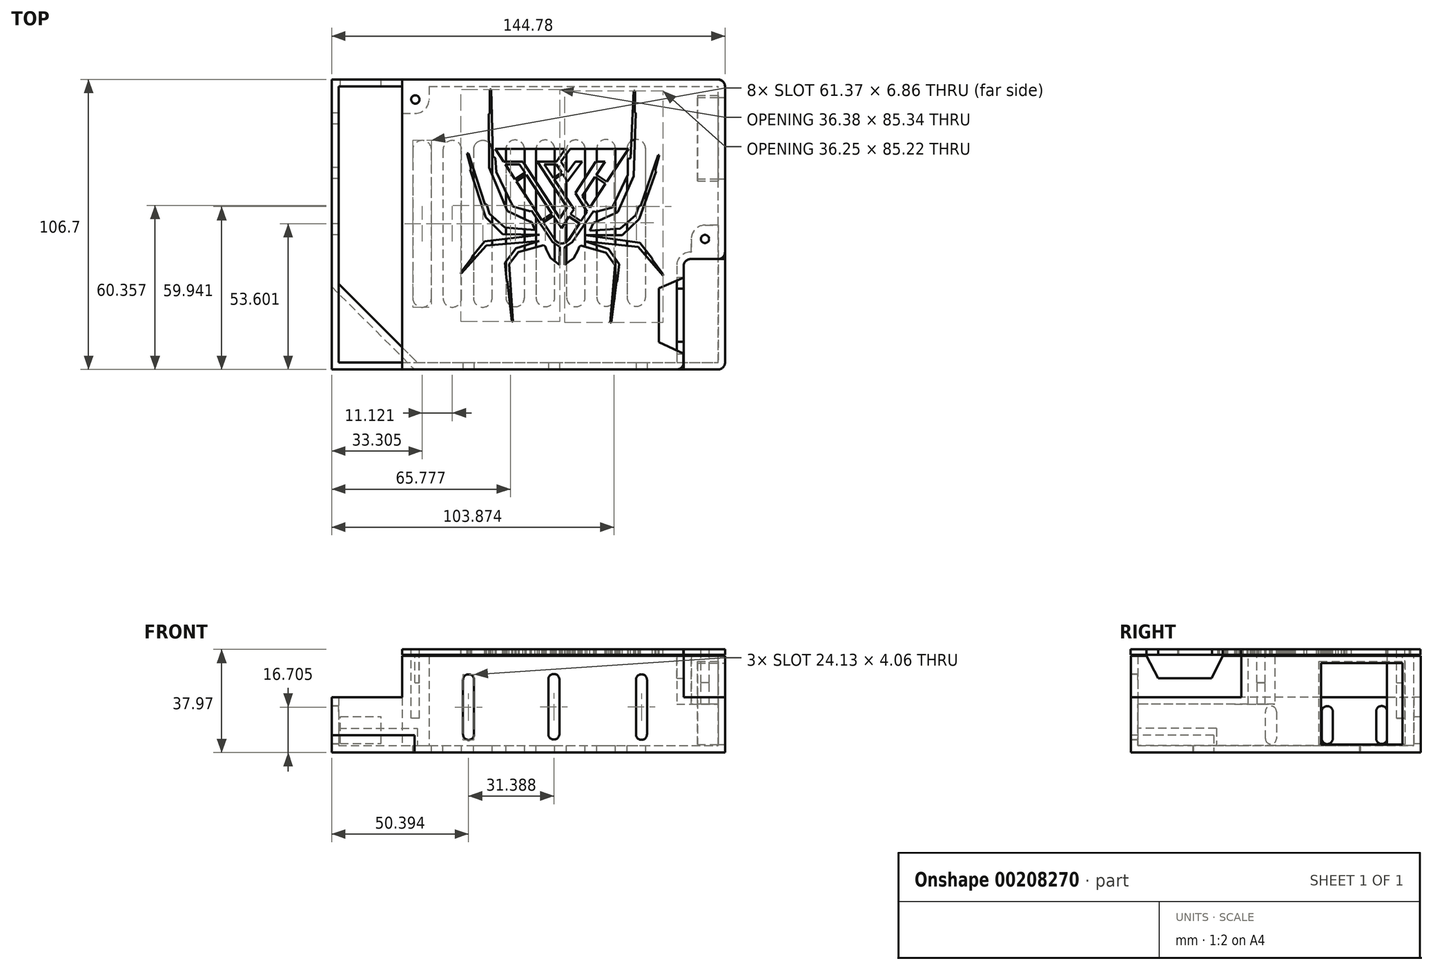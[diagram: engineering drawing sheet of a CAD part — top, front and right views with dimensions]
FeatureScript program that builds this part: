
annotation { "Feature Type Name" : "Feature", "Feature Type Description" : "" }
export const myFeature = defineFeature(function(context is Context, id is Id, definition is map)
    precondition{}
    {
        {
            var Q0;
            Q0=qCreatedBy(makeId("Top.planeOp"),FACE);
            var sketch = newSketch(context, id + "F0", { "sketchPlane" : qUnion([Q0])});
            skLineSegment(sketch, "E0", {"start": v(-77.03, 67.5) * mm, "end": v(67.75, 67.5) * mm});
            skLineSegment(sketch, "E1", {"start": v(67.75, 67.5) * mm, "end": v(67.75, -39.17) * mm});
            skLineSegment(sketch, "E2", {"start": v(-77.03, 67.5) * mm, "end": v(-77.03, -39.17) * mm});
            skLineSegment(sketch, "E3", {"start": v(-77.03, -39.17) * mm, "end": v(67.75, -39.17) * mm});
            skSolve(sketch);
        }
        {
            var Q0;
            Q0 = qSketchRegion(id + "F0", true);
            extrude(context, id + "F1", {"entities" : qUnion([Q0]), "depth" : 35.56 * mm, "offsetDistance" : 25.4 * mm});
        }
        {
            var Q0;
            Q0=makeQuery(id+"F1.opExtrude","CAP_FACE",FACE,{"disambiguationData":[OSD([sQuery(id+"F0.wireOp",EDGE,"E0"),sQuery(id+"F0.wireOp",EDGE,"E1"),sQuery(id+"F0.wireOp",EDGE,"E2"),sQuery(id+"F0.wireOp",EDGE,"E3")])],"isStart":true});
            var sketch = newSketch(context, id + "F2", { "sketchPlane" : qUnion([Q0])});
            skLineSegment(sketch, "E4", {"start": v(-77.03, 39.17) * mm, "end": v(-46.55, 39.17) * mm});
            skLineSegment(sketch, "E5", {"start": v(-77.03, 39.17) * mm, "end": v(-77.03, 8.7) * mm});
            skLineSegment(sketch, "E6", {"start": v(-77.03, 8.7) * mm, "end": v(-46.55, 39.17) * mm});
            skSolve(sketch);
        }
        {
            var Q0;
            Q0 = qSketchRegion(id + "F2", true);
            extrude(context, id + "F3", {"entities" : qUnion([Q0]), "operationType" : NewBodyOperationType.REMOVE, "oppositeDirection" : true, "depth" : 6.35 * mm});
        }
        {
            var Q0;
            Q0=makeQuery(id+"F1.opExtrude","SWEPT_FACE",FACE,{"disambiguationData":[OSD([sQuery(id+"F0.wireOp",EDGE,"E3")])]});
            var sketch = newSketch(context, id + "F4", { "sketchPlane" : qUnion([Q0])});
            skLineSegment(sketch, "E7", {"start": v(67.75, 35.56) * mm, "end": v(52.5, 35.56) * mm});
            skLineSegment(sketch, "E8", {"start": v(52.5, 35.56) * mm, "end": v(52.5, 20.32) * mm});
            skLineSegment(sketch, "E9", {"start": v(52.5, 20.32) * mm, "end": v(67.75, 20.32) * mm});
            skLineSegment(sketch, "E10", {"start": v(67.75, 20.32) * mm, "end": v(67.75, 35.56) * mm});
            skSolve(sketch);
        }
        {
            var Q0;
            Q0 = qSketchRegion(id + "F4", true);
            extrude(context, id + "F5", {"entities" : qUnion([Q0]), "operationType" : NewBodyOperationType.REMOVE, "oppositeDirection" : true, "depth" : 40.64 * mm});
        }
        {
            var Q0;
            Q0=makeQuery(id+"F1.opExtrude","SWEPT_EDGE",EDGE,{"disambiguationData":[OSD([sQuery(id+"F0.wireOp",EDGE,"E1"),sQuery(id+"F0.wireOp",EDGE,"E3")])]});
            var Q1;
            Q1=makeQuery(id+"F5.boolean.opBoolean","COPY",EDGE,{"derivedFrom":makeQuery(id+"F5.opExtrude","CAP_EDGE",EDGE,{"disambiguationData":[OSD([sQuery(id+"F4.wireOp",EDGE,"E8")])],"isStart":true})});
            var Q2;
            Q2=makeQuery(id+"F5.boolean.opBoolean","COPY",EDGE,{"derivedFrom":makeQuery(id+"F5.opExtrude","CAP_EDGE",EDGE,{"disambiguationData":[OSD([sQuery(id+"F4.wireOp",EDGE,"E10")])],"isStart":false})});
            var Q3;
            Q3=makeQuery(id+"F1.opExtrude","SWEPT_EDGE",EDGE,{"disambiguationData":[OSD([sQuery(id+"F0.wireOp",EDGE,"E0"),sQuery(id+"F0.wireOp",EDGE,"E1")])]});
            var Q4;
            Q4=makeQuery(id+"F5.boolean.opBoolean","COPY",EDGE,{"derivedFrom":makeQuery(id+"F5.opExtrude","CAP_EDGE",EDGE,{"disambiguationData":[OSD([sQuery(id+"F4.wireOp",EDGE,"E8")])],"isStart":false})});
            fillet(context, id + "F6", {"entities" : qUnion([Q0, Q1, Q2, Q3, Q4]), "radius" : 2.54 * mm, "tangentPropagation" : true, "allowEdgeOverflow" : false});
        }
        {
            var Q0;
            Q0=makeQuery(id+"F1.opExtrude","CAP_FACE",FACE,{"disambiguationData":[OSD([sQuery(id+"F0.wireOp",EDGE,"E0"),sQuery(id+"F0.wireOp",EDGE,"E1"),sQuery(id+"F0.wireOp",EDGE,"E2"),sQuery(id+"F0.wireOp",EDGE,"E3")])],"isStart":false});
            shell(context, id + "F7", {"entities" : qUnion([Q0]), "thickness" : 2.54 * mm});
        }
        {
            var Q0;
            Q0=makeQuery(id+"F1.opExtrude","SWEPT_FACE",FACE,{"disambiguationData":[OSD([sQuery(id+"F0.wireOp",EDGE,"E3")])]});
            var sketch = newSketch(context, id + "F8", { "sketchPlane" : qUnion([Q0])});
            skLineSegment(sketch, "E11", {"start": v(-77.03, 20.32) * mm, "end": v(-51.05, 20.32) * mm});
            skLineSegment(sketch, "E12", {"start": v(-51.05, 20.32) * mm, "end": v(-51.05, 35.56) * mm});
            skLineSegment(sketch, "E13", {"start": v(-51.05, 35.56) * mm, "end": v(-77.03, 35.56) * mm});
            skLineSegment(sketch, "E14", {"start": v(-77.03, 35.56) * mm, "end": v(-77.03, 20.32) * mm});
            skSolve(sketch);
        }
        {
            var Q0;
            Q0 = qSketchRegion(id + "F8", true);
            extrude(context, id + "F9", {"entities" : qUnion([Q0]), "operationType" : NewBodyOperationType.REMOVE, "oppositeDirection" : true, "depth" : 148.08 * mm});
        }
        {
            var Q0;
            Q0=makeQuery(id+"F5.boolean.opBoolean","COPY",FACE,{"derivedFrom":makeQuery(id+"F5.opExtrude","SWEPT_FACE",FACE,{"disambiguationData":[OSD([sQuery(id+"F4.wireOp",EDGE,"E8")])]})});
            var sketch = newSketch(context, id + "F10", { "sketchPlane" : qUnion([Q0])});
            skLineSegment(sketch, "E15", {"start": v(-33.43, 35.56) * mm, "end": v(-29.05, 27.26) * mm});
            skLineSegment(sketch, "E16", {"start": v(-29.05, 27.26) * mm, "end": v(-9.4, 27.26) * mm});
            skLineSegment(sketch, "E17", {"start": v(-9.4, 27.26) * mm, "end": v(-5.3, 35.56) * mm});
            skLineSegment(sketch, "E18", {"start": v(-5.3, 35.56) * mm, "end": v(-33.43, 35.56) * mm});
            skSolve(sketch);
        }
        {
            var Q0;
            Q0 = qSketchRegion(id + "F10", true);
            extrude(context, id + "F11", {"entities" : qUnion([Q0]), "operationType" : NewBodyOperationType.REMOVE, "oppositeDirection" : true, "depth" : 25.4 * mm});
        }
        {
            var Q0;
            Q0=makeQuery(id+"F1.opExtrude","SWEPT_FACE",FACE,{"disambiguationData":[OSD([sQuery(id+"F0.wireOp",EDGE,"E1")])]});
            var sketch = newSketch(context, id + "F12", { "sketchPlane" : qUnion([Q0])});
            skLineSegment(sketch, "E19.bottom", {"start": v(60.88, 32.96) * mm, "end": v(30.9, 32.96) * mm});
            skLineSegment(sketch, "E19.top", {"start": v(60.88, 2.99) * mm, "end": v(30.9, 2.99) * mm});
            skLineSegment(sketch, "E19.left", {"start": v(60.88, 32.96) * mm, "end": v(60.88, 2.99) * mm});
            skLineSegment(sketch, "E19.right", {"start": v(30.9, 32.96) * mm, "end": v(30.9, 2.99) * mm});
            skSolve(sketch);
        }
        {
            var Q0;
            Q0 = qSketchRegion(id + "F12", true);
            extrude(context, id + "F13", {"entities" : qUnion([Q0]), "operationType" : NewBodyOperationType.REMOVE, "oppositeDirection" : true, "depth" : 25.4 * mm});
        }
        {
            var Q0;
            Q0=makeQuery(id+"F7.opShell","OFFSET_FACE",FACE,{"disambiguationData":[OSD([sQuery(id+"F0.wireOp",EDGE,"E1")])]});
            var sketch = newSketch(context, id + "F14", { "sketchPlane" : qUnion([Q0])});
            skLineSegment(sketch, "E20", {"start": v(-60.88, 32.96) * mm, "end": v(-30.9, 32.96) * mm});
            skLineSegment(sketch, "E21", {"start": v(-30.9, 32.96) * mm, "end": v(-30.9, 2.99) * mm});
            skLineSegment(sketch, "E22", {"start": v(-30.9, 2.99) * mm, "end": v(-30.16, 2.99) * mm});
            skLineSegment(sketch, "E23", {"start": v(-30.16, 2.99) * mm, "end": v(-30.16, 33.5) * mm});
            skLineSegment(sketch, "E24", {"start": v(-30.16, 33.5) * mm, "end": v(-61.7, 33.5) * mm});
            skLineSegment(sketch, "E25", {"start": v(-61.7, 33.5) * mm, "end": v(-61.7, 2.99) * mm});
            skLineSegment(sketch, "E26", {"start": v(-61.7, 2.99) * mm, "end": v(-60.88, 2.99) * mm});
            skLineSegment(sketch, "E27", {"start": v(-60.88, 2.99) * mm, "end": v(-60.88, 32.96) * mm});
            skSolve(sketch);
        }
        {
            var Q0;
            Q0 = qSketchRegion(id + "F14", true);
            extrude(context, id + "F15", {"entities" : qUnion([Q0]), "operationType" : NewBodyOperationType.ADD, "depth" : 7.62 * mm});
        }
        {
            var Q0;
            Q0=makeQuery(id+"F7.opShell","OFFSET_FACE",FACE,{"disambiguationData":[OSD([sQuery(id+"F0.wireOp",EDGE,"E0"),sQuery(id+"F0.wireOp",EDGE,"E1"),sQuery(id+"F0.wireOp",EDGE,"E2"),sQuery(id+"F0.wireOp",EDGE,"E3")])]});
            var sketch = newSketch(context, id + "F16", { "sketchPlane" : qUnion([Q0])});
            skLineSegment(sketch, "E28.bottom", {"start": v(55.31, 13.9) * mm, "end": v(65.22, 13.9) * mm});
            skLineSegment(sketch, "E28.top", {"start": v(55.31, 4) * mm, "end": v(65.22, 4) * mm});
            skLineSegment(sketch, "E28.left", {"start": v(55.31, 13.9) * mm, "end": v(55.31, 4) * mm});
            skLineSegment(sketch, "E28.right", {"start": v(65.22, 13.9) * mm, "end": v(65.22, 4) * mm});
            skLineSegment(sketch, "E29.bottom", {"start": v(-51.05, 64.99) * mm, "end": v(-41.15, 64.99) * mm});
            skLineSegment(sketch, "E29.top", {"start": v(-51.05, 55.08) * mm, "end": v(-41.15, 55.08) * mm});
            skLineSegment(sketch, "E29.left", {"start": v(-51.05, 64.99) * mm, "end": v(-51.05, 55.08) * mm});
            skLineSegment(sketch, "E29.right", {"start": v(-41.15, 64.99) * mm, "end": v(-41.15, 55.08) * mm});
            skSolve(sketch);
        }
        {
            var Q0;
            Q0 = qSketchRegion(id + "F16", true);
            extrude(context, id + "F17", {"entities" : qUnion([Q0]), "operationType" : NewBodyOperationType.ADD, "depth" : 33.02 * mm});
        }
        {
            var Q0;
            Q0=makeQuery(id+"F17.opExtrude","SWEPT_FACE",FACE,{"disambiguationData":[OSD([sQuery(id+"F16.wireOp",EDGE,"E28.left")])]});
            var sketch = newSketch(context, id + "F18", { "sketchPlane" : qUnion([Q0])});
            skLineSegment(sketch, "E30", {"start": v(-4, 2.54) * mm, "end": v(-4, 17.78) * mm});
            skLineSegment(sketch, "E31", {"start": v(-4, 17.78) * mm, "end": v(-13.9, 17.78) * mm});
            skLineSegment(sketch, "E32", {"start": v(-13.9, 17.78) * mm, "end": v(-13.9, 2.54) * mm});
            skLineSegment(sketch, "E33", {"start": v(-13.9, 2.54) * mm, "end": v(-4, 2.54) * mm});
            skSolve(sketch);
        }
        {
            var Q0;
            Q0 = qSketchRegion(id + "F18", true);
            extrude(context, id + "F19", {"entities" : qUnion([Q0]), "operationType" : NewBodyOperationType.REMOVE, "oppositeDirection" : true, "depth" : 9.9 * mm});
        }
        {
            var Q0;
            Q0=makeQuery(id+"F17.opExtrude","SWEPT_EDGE",EDGE,{"disambiguationData":[OSD([sQuery(id+"F16.wireOp",EDGE,"E29.top"),sQuery(id+"F16.wireOp",EDGE,"E29.right")])]});
            var Q1;
            Q1=makeQuery(id+"F17.opExtrude","SWEPT_EDGE",EDGE,{"disambiguationData":[OSD([sQuery(id+"F16.wireOp",EDGE,"E28.bottom"),sQuery(id+"F16.wireOp",EDGE,"E28.left")])]});
            fillet(context, id + "F20", {"entities" : qUnion([Q0, Q1]), "radius" : 5.08 * mm, "tangentPropagation" : true, "allowEdgeOverflow" : false});
        }
        {
            var Q0;
            {var subQ2=sQuery(id+"F0.wireOp",EDGE,"E0");var subQ7=sQuery(id+"F0.wireOp",EDGE,"E1");var subQ8=makeQuery(id+"F1.opExtrude","SWEPT_FACE",FACE,{"disambiguationData":[OSD([subQ2])]});var subQ10=makeQuery(id+"F1.opExtrude","CAP_FACE",FACE,{"disambiguationData":[OSD([subQ2,subQ7,sQuery(id+"F0.wireOp",EDGE,"E2"),sQuery(id+"F0.wireOp",EDGE,"E3")])],"isStart":false});Q0=makeQuery(id+"F17.boolean.opBoolean","MERGE",FACE,{"derivedFrom":[makeQuery(id+"F11.boolean.opBoolean","SPLIT",FACE,{"disambiguationData":[TD([subQ8])],"derivedFrom":subQ10}),makeQuery(id+"F17.opExtrude","CAP_FACE",FACE,{"disambiguationData":[OSD([sQuery(id+"F16.wireOp",EDGE,"E28.bottom"),sQuery(id+"F16.wireOp",EDGE,"E28.top"),sQuery(id+"F16.wireOp",EDGE,"E28.left"),sQuery(id+"F16.wireOp",EDGE,"E28.right")])],"isStart":false}),makeQuery(id+"F17.opExtrude","CAP_FACE",FACE,{"disambiguationData":[OSD([sQuery(id+"F16.wireOp",EDGE,"E29.bottom"),sQuery(id+"F16.wireOp",EDGE,"E29.top"),sQuery(id+"F16.wireOp",EDGE,"E29.left"),sQuery(id+"F16.wireOp",EDGE,"E29.right")])],"isStart":false})]});}
            var sketch = newSketch(context, id + "F21", { "sketchPlane" : qUnion([Q0])});
            skCircle(sketch, "E34", {"center": v(-46.23, 60.16) * mm, "radius": 1.52 * mm});
            skCircle(sketch, "E35", {"center": v(60.4, 8.83) * mm, "radius": 1.52 * mm});
            skSolve(sketch);
        }
        {
            var Q0;
            Q0 = qSketchRegion(id + "F21", true);
            extrude(context, id + "F22", {"entities" : qUnion([Q0]), "operationType" : NewBodyOperationType.REMOVE, "oppositeDirection" : true, "depth" : 9.9 * mm});
        }
        {
            var Q0;
            Q0=makeQuery(id+"F1.opExtrude","SWEPT_FACE",FACE,{"disambiguationData":[OSD([sQuery(id+"F0.wireOp",EDGE,"E0")])]});
            var sketch = newSketch(context, id + "F23", { "sketchPlane" : qUnion([Q0])});
            skLineSegment(sketch, "E36.bottom", {"start": v(73.84, 3.33) * mm, "end": v(58.85, 3.33) * mm});
            skLineSegment(sketch, "E36.top", {"start": v(73.84, 13.24) * mm, "end": v(58.85, 13.24) * mm});
            skLineSegment(sketch, "E36.left", {"start": v(73.84, 3.33) * mm, "end": v(73.84, 13.24) * mm});
            skLineSegment(sketch, "E36.right", {"start": v(58.85, 3.33) * mm, "end": v(58.85, 13.24) * mm});
            skSolve(sketch);
        }
        {
            var Q0;
            Q0 = qSketchRegion(id + "F23", true);
            extrude(context, id + "F24", {"entities" : qUnion([Q0]), "operationType" : NewBodyOperationType.REMOVE, "oppositeDirection" : true, "depth" : 25.4 * mm});
        }
        {
            var Q0;
            Q0=makeQuery(id+"F19.boolean.opBoolean","MERGE",FACE,{"derivedFrom":[makeQuery(id+"F7.opShell","OFFSET_FACE",FACE,{"disambiguationData":[OSD([sQuery(id+"F0.wireOp",EDGE,"E0"),sQuery(id+"F0.wireOp",EDGE,"E1"),sQuery(id+"F0.wireOp",EDGE,"E2"),sQuery(id+"F0.wireOp",EDGE,"E3")])]}),makeQuery(id+"F19.opExtrude","SWEPT_FACE",FACE,{"disambiguationData":[OSD([sQuery(id+"F18.wireOp",EDGE,"E33")])]})]});
            var sketch = newSketch(context, id + "F25", { "sketchPlane" : qUnion([Q0])});
            skLineSegment(sketch, "E37", {"start": v(-47.15, 41.67) * mm, "end": v(-47.15, -12.85) * mm});
            skLineSegment(sketch, "E38", {"start": v(-40.3, -12.85) * mm, "end": v(-40.3, 41.67) * mm});
            skArc(sketch, "E39", {"start": v(-40.3, 41.67) * mm, "mid": v(-43.73, 45.1) * mm, "end": v(-47.15, 41.67) * mm});
            skArc(sketch, "E40", {"start": v(-47.15, -12.85) * mm, "mid": v(-43.73, -16.27) * mm, "end": v(-40.3, -12.85) * mm});
            skLineSegment(sketch, "E41", {"start": v(-36.03, 41.67) * mm, "end": v(-36.03, -12.85) * mm});
            skLineSegment(sketch, "E42", {"start": v(-29.18, -12.85) * mm, "end": v(-29.18, 41.67) * mm});
            skArc(sketch, "E43", {"start": v(-29.18, 41.67) * mm, "mid": v(-32.6, 45.1) * mm, "end": v(-36.03, 41.67) * mm});
            skArc(sketch, "E44", {"start": v(-36.03, -12.85) * mm, "mid": v(-32.6, -16.27) * mm, "end": v(-29.18, -12.85) * mm});
            skLineSegment(sketch, "E45", {"start": v(-24.83, 41.67) * mm, "end": v(-24.83, -12.85) * mm});
            skLineSegment(sketch, "E46", {"start": v(-17.97, -12.85) * mm, "end": v(-17.97, 41.67) * mm});
            skArc(sketch, "E47", {"start": v(-17.97, 41.67) * mm, "mid": v(-21.4, 45.1) * mm, "end": v(-24.83, 41.67) * mm});
            skArc(sketch, "E48", {"start": v(-24.83, -12.85) * mm, "mid": v(-21.4, -16.27) * mm, "end": v(-17.97, -12.85) * mm});
            skLineSegment(sketch, "E49", {"start": v(-12.9, 41.83) * mm, "end": v(-12.9, -12.68) * mm});
            skLineSegment(sketch, "E50", {"start": v(-6.04, -12.68) * mm, "end": v(-6.04, 41.83) * mm});
            skArc(sketch, "E51", {"start": v(-6.04, 41.83) * mm, "mid": v(-9.47, 45.26) * mm, "end": v(-12.9, 41.83) * mm});
            skArc(sketch, "E52", {"start": v(-12.9, -12.68) * mm, "mid": v(-9.47, -16.1) * mm, "end": v(-6.04, -12.68) * mm});
            skLineSegment(sketch, "E53", {"start": v(-1.78, 41.83) * mm, "end": v(-1.78, -12.68) * mm});
            skLineSegment(sketch, "E54", {"start": v(5.08, -12.68) * mm, "end": v(5.08, 41.83) * mm});
            skArc(sketch, "E55", {"start": v(5.08, 41.83) * mm, "mid": v(1.65, 45.26) * mm, "end": v(-1.78, 41.83) * mm});
            skArc(sketch, "E56", {"start": v(-1.78, -12.68) * mm, "mid": v(1.65, -16.1) * mm, "end": v(5.08, -12.68) * mm});
            skLineSegment(sketch, "E57", {"start": v(9.43, 41.83) * mm, "end": v(9.43, -12.68) * mm});
            skLineSegment(sketch, "E58", {"start": v(16.28, -12.68) * mm, "end": v(16.28, 41.83) * mm});
            skArc(sketch, "E59", {"start": v(16.28, 41.83) * mm, "mid": v(12.86, 45.26) * mm, "end": v(9.43, 41.83) * mm});
            skArc(sketch, "E60", {"start": v(9.43, -12.68) * mm, "mid": v(12.86, -16.1) * mm, "end": v(16.28, -12.68) * mm});
            skLineSegment(sketch, "E61", {"start": v(20.55, 42) * mm, "end": v(20.55, -12.51) * mm});
            skLineSegment(sketch, "E62", {"start": v(27.4, -12.51) * mm, "end": v(27.4, 42) * mm});
            skArc(sketch, "E63", {"start": v(27.4, 42) * mm, "mid": v(23.98, 45.43) * mm, "end": v(20.55, 42) * mm});
            skArc(sketch, "E64", {"start": v(20.55, -12.51) * mm, "mid": v(23.98, -15.94) * mm, "end": v(27.4, -12.51) * mm});
            skLineSegment(sketch, "E65", {"start": v(31.67, 42) * mm, "end": v(31.67, -12.51) * mm});
            skLineSegment(sketch, "E66", {"start": v(38.53, -12.51) * mm, "end": v(38.53, 42) * mm});
            skArc(sketch, "E67", {"start": v(38.53, 42) * mm, "mid": v(35.1, 45.43) * mm, "end": v(31.67, 42) * mm});
            skArc(sketch, "E68", {"start": v(31.67, -12.51) * mm, "mid": v(35.1, -15.94) * mm, "end": v(38.53, -12.51) * mm});
            skSolve(sketch);
        }
        {
            var Q0;
            Q0 = qSketchRegion(id + "F25", true);
            extrude(context, id + "F26", {"entities" : qUnion([Q0]), "operationType" : NewBodyOperationType.REMOVE, "oppositeDirection" : true, "depth" : 25.4 * mm});
        }
        {
            var Q0;
            Q0=makeQuery(id+"F1.opExtrude","SWEPT_FACE",FACE,{"disambiguationData":[OSD([sQuery(id+"F0.wireOp",EDGE,"E3")])]});
            var sketch = newSketch(context, id + "F27", { "sketchPlane" : qUnion([Q0])});
            skLineSegment(sketch, "E69", {"start": v(-28.67, 26.74) * mm, "end": v(-28.67, 6.67) * mm});
            skLineSegment(sketch, "E70", {"start": v(-24.6, 6.67) * mm, "end": v(-24.6, 26.74) * mm});
            skArc(sketch, "E71", {"start": v(-24.6, 26.74) * mm, "mid": v(-26.64, 28.77) * mm, "end": v(-28.67, 26.74) * mm});
            skArc(sketch, "E72", {"start": v(-28.67, 6.67) * mm, "mid": v(-26.64, 4.64) * mm, "end": v(-24.6, 6.67) * mm});
            skLineSegment(sketch, "E73", {"start": v(34.98, 26.76) * mm, "end": v(34.98, 6.7) * mm});
            skLineSegment(sketch, "E74", {"start": v(39.04, 6.7) * mm, "end": v(39.04, 26.76) * mm});
            skArc(sketch, "E75", {"start": v(39.04, 26.76) * mm, "mid": v(37, 28.8) * mm, "end": v(34.98, 26.76) * mm});
            skArc(sketch, "E76", {"start": v(34.98, 6.7) * mm, "mid": v(37, 4.66) * mm, "end": v(39.04, 6.7) * mm});
            skLineSegment(sketch, "E77", {"start": v(2.72, 26.87) * mm, "end": v(2.72, 6.8) * mm});
            skLineSegment(sketch, "E78", {"start": v(6.78, 6.8) * mm, "end": v(6.78, 26.87) * mm});
            skArc(sketch, "E79", {"start": v(6.78, 26.87) * mm, "mid": v(4.75, 28.9) * mm, "end": v(2.72, 26.87) * mm});
            skArc(sketch, "E80", {"start": v(2.72, 6.8) * mm, "mid": v(4.75, 4.77) * mm, "end": v(6.78, 6.8) * mm});
            skSolve(sketch);
        }
        {
            var Q0;
            Q0 = qSketchRegion(id + "F27", true);
            extrude(context, id + "F28", {"entities" : qUnion([Q0]), "operationType" : NewBodyOperationType.REMOVE, "oppositeDirection" : true, "depth" : 25.4 * mm});
        }
        {
            var Q0;
            Q0=makeQuery(id+"F1.opExtrude","SWEPT_FACE",FACE,{"disambiguationData":[OSD([sQuery(id+"F0.wireOp",EDGE,"E2")])]});
            var sketch = newSketch(context, id + "F29", { "sketchPlane" : qUnion([Q0])});
            skLineSegment(sketch, "E81", {"start": v(-55.2, 15.1) * mm, "end": v(-55.2, 5.19) * mm});
            skLineSegment(sketch, "E82", {"start": v(-51.13, 5.19) * mm, "end": v(-51.13, 15.1) * mm});
            skArc(sketch, "E83", {"start": v(-51.13, 15.1) * mm, "mid": v(-53.16, 17.13) * mm, "end": v(-55.2, 15.1) * mm});
            skArc(sketch, "E84", {"start": v(-55.2, 5.19) * mm, "mid": v(-53.16, 3.16) * mm, "end": v(-51.13, 5.19) * mm});
            skLineSegment(sketch, "E85", {"start": v(-14.45, 15.05) * mm, "end": v(-14.45, 5.14) * mm});
            skLineSegment(sketch, "E86", {"start": v(-10.38, 5.14) * mm, "end": v(-10.38, 15.05) * mm});
            skArc(sketch, "E87", {"start": v(-10.38, 15.05) * mm, "mid": v(-12.42, 17.08) * mm, "end": v(-14.45, 15.05) * mm});
            skArc(sketch, "E88", {"start": v(-14.45, 5.14) * mm, "mid": v(-12.42, 3.1) * mm, "end": v(-10.38, 5.14) * mm});
            skLineSegment(sketch, "E89", {"start": v(-35.16, 15.05) * mm, "end": v(-35.16, 5.14) * mm});
            skLineSegment(sketch, "E90", {"start": v(-31.1, 5.14) * mm, "end": v(-31.1, 15.05) * mm});
            skArc(sketch, "E91", {"start": v(-31.1, 15.05) * mm, "mid": v(-33.13, 17.08) * mm, "end": v(-35.16, 15.05) * mm});
            skArc(sketch, "E92", {"start": v(-35.16, 5.14) * mm, "mid": v(-33.13, 3.1) * mm, "end": v(-31.1, 5.14) * mm});
            skSolve(sketch);
        }
        {
            var Q0;
            Q0 = qSketchRegion(id + "F29", true);
            extrude(context, id + "F30", {"entities" : qUnion([Q0]), "operationType" : NewBodyOperationType.REMOVE, "oppositeDirection" : true, "depth" : 25.4 * mm});
        }
        {
            var Q0;
            Q0=qCreatedBy(makeId("Top.planeOp"),FACE);
            cPlane(context, id + "F31", {"entities" : qUnion([Q0]), "cplaneType" : CPlaneType.OFFSET, "offset" : 35.94 * mm, "width" : 152.4 * mm, "height" : 152.4 * mm});
        }
        {
            var Q0;
            Q0=qCreatedBy(id+"F31.planeOp",FACE);
            var sketch = newSketch(context, id + "F32", { "sketchPlane" : qUnion([Q0])});
            skLineSegment(sketch, "E93", {"start": v(-51.08, 67.49) * mm, "end": v(67.74, 67.49) * mm});
            skLineSegment(sketch, "E94", {"start": v(67.74, 67.49) * mm, "end": v(67.74, 1.43) * mm});
            skLineSegment(sketch, "E95", {"start": v(67.74, 1.43) * mm, "end": v(52.55, 1.43) * mm});
            skLineSegment(sketch, "E96", {"start": v(52.49, -39.2) * mm, "end": v(-51.08, -39.2) * mm});
            skLineSegment(sketch, "E97", {"start": v(-51.08, -39.2) * mm, "end": v(-51.08, 67.49) * mm});
            skLineSegment(sketch, "E98", {"start": v(52.55, -5.35) * mm, "end": v(43.4, -9.27) * mm});
            skLineSegment(sketch, "E99", {"start": v(52.49, -33.38) * mm, "end": v(43.4, -29.1) * mm});
            skLineSegment(sketch, "E100", {"start": v(43.4, -29.1) * mm, "end": v(43.4, -9.27) * mm});
            skLineSegment(sketch, "E101", {"start": v(52.55, -5.35) * mm, "end": v(52.55, 1.43) * mm});
            skLineSegment(sketch, "E102", {"start": v(52.49, -33.38) * mm, "end": v(52.49, -39.2) * mm});
            skSolve(sketch);
        }
        {
            var Q0;
            Q0 = qSketchRegion(id + "F32", true);
            extrude(context, id + "F33", {"entities" : qUnion([Q0]), "depth" : 2.03 * mm});
        }
        {
            var Q0;
            Q0=makeQuery(id+"F33.opExtrude","SWEPT_EDGE",EDGE,{"disambiguationData":[OSD([sQuery(id+"F32.wireOp",EDGE,"E96"),sQuery(id+"F32.wireOp",EDGE,"E102")])]});
            var Q1;
            Q1=makeQuery(id+"F33.opExtrude","SWEPT_EDGE",EDGE,{"disambiguationData":[OSD([sQuery(id+"F32.wireOp",EDGE,"E94"),sQuery(id+"F32.wireOp",EDGE,"E95")])]});
            var Q2;
            Q2=makeQuery(id+"F33.opExtrude","SWEPT_EDGE",EDGE,{"disambiguationData":[OSD([sQuery(id+"F32.wireOp",EDGE,"E95"),sQuery(id+"F32.wireOp",EDGE,"E101")])]});
            var Q3;
            Q3=makeQuery(id+"F33.opExtrude","SWEPT_EDGE",EDGE,{"disambiguationData":[OSD([sQuery(id+"F32.wireOp",EDGE,"E93"),sQuery(id+"F32.wireOp",EDGE,"E94")])]});
            var Q4;
            Q4=makeQuery(id+"F33.opExtrude","SWEPT_EDGE",EDGE,{"disambiguationData":[OSD([sQuery(id+"F32.wireOp",EDGE,"E94"),sQuery(id+"F32.wireOp",EDGE,"E95")])]});
            fillet(context, id + "F34", {"entities" : qUnion([Q0, Q1, Q2, Q3, Q4]), "radius" : 2.54 * mm, "tangentPropagation" : true, "allowEdgeOverflow" : false});
        }
        {
            var Q0;
            Q0=makeQuery(id+"F33.opExtrude","CAP_FACE",FACE,{"disambiguationData":[OSD([sQuery(id+"F32.wireOp",EDGE,"E93"),sQuery(id+"F32.wireOp",EDGE,"E94"),sQuery(id+"F32.wireOp",EDGE,"E95"),sQuery(id+"F32.wireOp",EDGE,"E96"),sQuery(id+"F32.wireOp",EDGE,"E97"),sQuery(id+"F32.wireOp",EDGE,"E98"),sQuery(id+"F32.wireOp",EDGE,"E99"),sQuery(id+"F32.wireOp",EDGE,"E100"),sQuery(id+"F32.wireOp",EDGE,"E101"),sQuery(id+"F32.wireOp",EDGE,"E102")])],"isStart":false});
            var sketch = newSketch(context, id + "F35", { "sketchPlane" : qUnion([Q0])});
            skCircle(sketch, "E103", {"center": v(-46.24, 60.17) * mm, "radius": 1.53 * mm});
            skCircle(sketch, "E104", {"center": v(60.39, 8.82) * mm, "radius": 1.5 * mm});
            skSolve(sketch);
        }
        {
            var Q0;
            Q0 = qSketchRegion(id + "F35", true);
            extrude(context, id + "F36", {"entities" : qUnion([Q0]), "operationType" : NewBodyOperationType.REMOVE, "oppositeDirection" : true, "depth" : 25.4 * mm});
        }
        {
            var Q0;
            Q0=makeQuery(id+"F33.opExtrude","CAP_FACE",FACE,{"disambiguationData":[OSD([sQuery(id+"F32.wireOp",EDGE,"E93"),sQuery(id+"F32.wireOp",EDGE,"E94"),sQuery(id+"F32.wireOp",EDGE,"E95"),sQuery(id+"F32.wireOp",EDGE,"E96"),sQuery(id+"F32.wireOp",EDGE,"E97"),sQuery(id+"F32.wireOp",EDGE,"E98"),sQuery(id+"F32.wireOp",EDGE,"E99"),sQuery(id+"F32.wireOp",EDGE,"E100"),sQuery(id+"F32.wireOp",EDGE,"E101"),sQuery(id+"F32.wireOp",EDGE,"E102")])],"isStart":false});
            var sketch = newSketch(context, id + "F37", { "sketchPlane" : qUnion([Q0])});
            skPoint(sketch, "E105.endSnap0", {"position": v(7.67, 42.02) * mm});
            skLineSegment(sketch, "E106", {"start": v(-16.85, 42.02) * mm, "end": v(9.01, 42.02) * mm});
            skLineSegment(sketch, "E107", {"start": v(9.01, 42.02) * mm, "end": v(5.67, 37.23) * mm});
            skLineSegment(sketch, "E108", {"start": v(-16.85, 42.02) * mm, "end": v(-13.71, 37.23) * mm});
            skLineSegment(sketch, "E109", {"start": v(-13.1, 36.3) * mm, "end": v(-7.84, 36.3) * mm});
            skLineSegment(sketch, "E110", {"start": v(1.29, 36.3) * mm, "end": v(5.67, 36.3) * mm});
            skArc(sketch, "E111", {"start": v(4.91, 8.8) * mm, "mid": v(7.55, 7.2) * mm, "end": v(10.3, 8.62) * mm});
            skLineSegment(sketch, "E112", {"start": v(7.4, 37.23) * mm, "end": v(10.74, 42.02) * mm});
            skLineSegment(sketch, "E113", {"start": v(10.74, 42.02) * mm, "end": v(32.18, 42.02) * mm});
            skLineSegment(sketch, "E114", {"start": v(18, 20.38) * mm, "end": v(15.25, 24.58) * mm});
            skLineSegment(sketch, "E115", {"start": v(7.4, 37.23) * mm, "end": v(9.84, 33.5) * mm});
            skLineSegment(sketch, "E116", {"start": v(9.84, 33.5) * mm, "end": v(12.63, 37.23) * mm});
            skLineSegment(sketch, "E117", {"start": v(9.75, 30.06) * mm, "end": v(15.18, 37.23) * mm});
            skLineSegment(sketch, "E118", {"start": v(15.18, 37.23) * mm, "end": v(12.63, 37.23) * mm});
            skLineSegment(sketch, "E119", {"start": v(12.63, 25.67) * mm, "end": v(20.2, 37.23) * mm});
            skLineSegment(sketch, "E120", {"start": v(20.2, 37.23) * mm, "end": v(23.54, 37.23) * mm});
            skLineSegment(sketch, "E121", {"start": v(17.05, 18.93) * mm, "end": v(12.63, 25.67) * mm});
            skLineSegment(sketch, "E122", {"start": v(-13.71, 37.23) * mm, "end": v(-6.62, 37.23) * mm});
            skLineSegment(sketch, "E123", {"start": v(-6.62, 37.23) * mm, "end": v(7, 16.45) * mm});
            skLineSegment(sketch, "E124", {"start": v(7, 16.45) * mm, "end": v(9.68, 20.55) * mm});
            skLineSegment(sketch, "E125", {"start": v(9.68, 20.55) * mm, "end": v(-1.25, 37.23) * mm});
            skLineSegment(sketch, "E126", {"start": v(-1.25, 37.23) * mm, "end": v(5.67, 37.23) * mm});
            skLineSegment(sketch, "E127", {"start": v(10.9, 17.94) * mm, "end": v(14.75, 15.42) * mm});
            skLineSegment(sketch, "E128", {"start": v(10.3, 17.03) * mm, "end": v(14.15, 14.5) * mm});
            skLineSegment(sketch, "E129", {"start": v(4.55, 17.4) * mm, "end": v(0.87, 14.98) * mm});
            skLineSegment(sketch, "E130", {"start": v(0.36, 15.75) * mm, "end": v(4.04, 18.17) * mm});
            skLineSegment(sketch, "E131", {"start": v(-9.5, 30.79) * mm, "end": v(-5.8, 33.2) * mm});
            skLineSegment(sketch, "E132", {"start": v(-9.03, 30.08) * mm, "end": v(-5.35, 32.5) * mm});
            skLineSegment(sketch, "E133", {"start": v(4.56, 31.3) * mm, "end": v(7.62, 33.31) * mm});
            skLineSegment(sketch, "E134", {"start": v(4.96, 30.69) * mm, "end": v(8.03, 32.7) * mm});
            skLineSegment(sketch, "E135", {"start": v(19.92, 31.7) * mm, "end": v(23.77, 29.18) * mm});
            skLineSegment(sketch, "E136", {"start": v(20.4, 32.44) * mm, "end": v(24.25, 29.91) * mm});
            skLineSegment(sketch, "E137", {"start": v(-13.1, 36.3) * mm, "end": v(-9.5, 30.79) * mm});
            skLineSegment(sketch, "E138", {"start": v(-7.84, 36.3) * mm, "end": v(-5.8, 33.2) * mm});
            skLineSegment(sketch, "E139", {"start": v(-5.35, 32.5) * mm, "end": v(4.04, 18.17) * mm});
            skLineSegment(sketch, "E140", {"start": v(-9.03, 30.08) * mm, "end": v(0.36, 15.75) * mm});
            skLineSegment(sketch, "E141", {"start": v(4.55, 17.4) * mm, "end": v(7.55, 12.82) * mm});
            skLineSegment(sketch, "E142", {"start": v(0.87, 14.98) * mm, "end": v(4.91, 8.8) * mm});
            skLineSegment(sketch, "E143", {"start": v(12.1, 19.79) * mm, "end": v(4.96, 30.69) * mm});
            skLineSegment(sketch, "E144", {"start": v(4.56, 31.3) * mm, "end": v(1.29, 36.3) * mm});
            skLineSegment(sketch, "E145", {"start": v(5.67, 36.3) * mm, "end": v(7.62, 33.31) * mm});
            skLineSegment(sketch, "E146", {"start": v(8.03, 32.7) * mm, "end": v(9.75, 30.06) * mm});
            skLineSegment(sketch, "E147", {"start": v(32.18, 42.02) * mm, "end": v(24.25, 29.91) * mm});
            skLineSegment(sketch, "E148", {"start": v(23.77, 29.18) * mm, "end": v(18, 20.38) * mm});
            skLineSegment(sketch, "E149", {"start": v(20.4, 32.44) * mm, "end": v(23.54, 37.23) * mm});
            skLineSegment(sketch, "E150", {"start": v(19.92, 31.7) * mm, "end": v(15.25, 24.58) * mm});
            skLineSegment(sketch, "E151", {"start": v(12.1, 19.79) * mm, "end": v(10.9, 17.94) * mm});
            skLineSegment(sketch, "E152", {"start": v(10.3, 17.03) * mm, "end": v(7.55, 12.82) * mm});
            skLineSegment(sketch, "E153", {"start": v(14.15, 14.5) * mm, "end": v(10.3, 8.62) * mm});
            skLineSegment(sketch, "E154", {"start": v(17.05, 18.93) * mm, "end": v(14.75, 15.42) * mm});
            skSolve(sketch);
        }
        {
            var Q0;
            Q0 = qSketchRegion(id + "F37", true);
            extrude(context, id + "F38", {"entities" : qUnion([Q0]), "operationType" : NewBodyOperationType.REMOVE, "oppositeDirection" : true, "depth" : 25.4 * mm});
        }
        {
            var Q0;
            Q0=makeQuery(id+"F33.opExtrude","CAP_FACE",FACE,{"disambiguationData":[OSD([sQuery(id+"F32.wireOp",EDGE,"E93"),sQuery(id+"F32.wireOp",EDGE,"E94"),sQuery(id+"F32.wireOp",EDGE,"E95"),sQuery(id+"F32.wireOp",EDGE,"E96"),sQuery(id+"F32.wireOp",EDGE,"E97"),sQuery(id+"F32.wireOp",EDGE,"E98"),sQuery(id+"F32.wireOp",EDGE,"E99"),sQuery(id+"F32.wireOp",EDGE,"E100"),sQuery(id+"F32.wireOp",EDGE,"E101"),sQuery(id+"F32.wireOp",EDGE,"E102")])],"isStart":false});
            var sketch = newSketch(context, id + "F39", { "sketchPlane" : qUnion([Q0])});
            skPoint(sketch, "E155.endSnap0", {"position": v(8.54, 25.24) * mm});
            skLineSegment(sketch, "E156", {"start": v(19.4, 19.08) * mm, "end": v(19.87, 18.77) * mm});
            skLineSegment(sketch, "E157", {"start": v(19.87, 18.77) * mm, "end": v(19.87, 18.7) * mm});
            skLineSegment(sketch, "E158", {"start": v(19.87, 18.7) * mm, "end": v(26.3, 20.38) * mm});
            skLineSegment(sketch, "E159", {"start": v(26.3, 20.38) * mm, "end": v(32.03, 32.47) * mm});
            skLineSegment(sketch, "E160", {"start": v(32.03, 32.47) * mm, "end": v(32.01, 38.3) * mm});
            skLineSegment(sketch, "E161", {"start": v(32.01, 38.3) * mm, "end": v(32.98, 38.53) * mm});
            skLineSegment(sketch, "E162", {"start": v(32.98, 38.53) * mm, "end": v(34.18, 63.36) * mm});
            skLineSegment(sketch, "E163", {"start": v(34.18, 63.36) * mm, "end": v(34.6, 63.34) * mm});
            skLineSegment(sketch, "E164", {"start": v(34.6, 63.34) * mm, "end": v(34.5, 55.45) * mm});
            skLineSegment(sketch, "E165", {"start": v(34.5, 55.45) * mm, "end": v(34.85, 55.14) * mm});
            skLineSegment(sketch, "E166", {"start": v(34.85, 55.14) * mm, "end": v(34.18, 31.9) * mm});
            skLineSegment(sketch, "E167", {"start": v(34.18, 31.9) * mm, "end": v(28.34, 18.7) * mm});
            skLineSegment(sketch, "E168", {"start": v(28.34, 18.7) * mm, "end": v(19.87, 14.92) * mm});
            skLineSegment(sketch, "E169", {"start": v(19.87, 14.92) * mm, "end": v(19.4, 14.93) * mm});
            skLineSegment(sketch, "E170", {"start": v(19.4, 14.93) * mm, "end": v(18, 11.92) * mm});
            skLineSegment(sketch, "E171", {"start": v(18, 11.92) * mm, "end": v(29.13, 12.59) * mm});
            skLineSegment(sketch, "E172", {"start": v(29.13, 12.59) * mm, "end": v(34.85, 17.61) * mm});
            skLineSegment(sketch, "E173", {"start": v(34.85, 17.61) * mm, "end": v(36.04, 20.97) * mm});
            skLineSegment(sketch, "E174", {"start": v(36.04, 20.97) * mm, "end": v(36.67, 20.95) * mm});
            skLineSegment(sketch, "E175", {"start": v(36.67, 20.95) * mm, "end": v(43.11, 39.69) * mm});
            skLineSegment(sketch, "E176", {"start": v(43.11, 39.69) * mm, "end": v(43.59, 39.68) * mm});
            skLineSegment(sketch, "E177", {"start": v(43.59, 39.68) * mm, "end": v(41.97, 33.98) * mm});
            skLineSegment(sketch, "E178", {"start": v(41.97, 33.98) * mm, "end": v(42.36, 33.7) * mm});
            skLineSegment(sketch, "E179", {"start": v(42.36, 33.7) * mm, "end": v(36.21, 16.25) * mm});
            skLineSegment(sketch, "E180", {"start": v(36.21, 16.25) * mm, "end": v(29.96, 10.2) * mm});
            skLineSegment(sketch, "E181", {"start": v(29.96, 10.2) * mm, "end": v(16.4, 10.2) * mm});
            skLineSegment(sketch, "E182", {"start": v(16.4, 10.2) * mm, "end": v(36.47, 7.39) * mm});
            skLineSegment(sketch, "E183", {"start": v(36.47, 7.39) * mm, "end": v(41.05, 1.63) * mm});
            skLineSegment(sketch, "E184", {"start": v(41.05, 1.63) * mm, "end": v(41.05, 1.2) * mm});
            skLineSegment(sketch, "E185", {"start": v(41.05, 1.2) * mm, "end": v(44.97, -4.18) * mm});
            skLineSegment(sketch, "E186", {"start": v(44.97, -4.18) * mm, "end": v(44.93, -4.64) * mm});
            skLineSegment(sketch, "E187", {"start": v(44.93, -4.64) * mm, "end": v(35.81, 5.93) * mm});
            skLineSegment(sketch, "E188", {"start": v(35.81, 5.93) * mm, "end": v(16.4, 7.92) * mm});
            skLineSegment(sketch, "E189", {"start": v(16.4, 7.92) * mm, "end": v(24.85, 5.09) * mm});
            skLineSegment(sketch, "E190", {"start": v(24.85, 5.09) * mm, "end": v(28.83, -0.38) * mm});
            skLineSegment(sketch, "E191", {"start": v(28.83, -0.38) * mm, "end": v(28, -6.9) * mm});
            skLineSegment(sketch, "E192", {"start": v(28, -6.9) * mm, "end": v(27.78, -7.05) * mm});
            skLineSegment(sketch, "E193", {"start": v(27.78, -7.05) * mm, "end": v(25.9, -21.86) * mm});
            skLineSegment(sketch, "E194", {"start": v(25.5, -21.86) * mm, "end": v(27.34, -0.87) * mm});
            skLineSegment(sketch, "E195", {"start": v(25.5, -21.86) * mm, "end": v(25.9, -21.86) * mm});
            skLineSegment(sketch, "E196", {"start": v(27.34, -0.87) * mm, "end": v(23.93, 3.74) * mm});
            skLineSegment(sketch, "E197", {"start": v(23.93, 3.74) * mm, "end": v(14.74, 6.47) * mm});
            skLineSegment(sketch, "E198", {"start": v(14.74, 6.47) * mm, "end": v(14.08, 5.97) * mm});
            skLineSegment(sketch, "E199", {"start": v(14.08, 5.97) * mm, "end": v(13.65, 4.8) * mm});
            skLineSegment(sketch, "E200", {"start": v(13.65, 4.8) * mm, "end": v(12.05, 1.7) * mm});
            skLineSegment(sketch, "E201", {"start": v(12.05, 1.7) * mm, "end": v(10.37, 0.58) * mm});
            skLineSegment(sketch, "E202", {"start": v(10.37, 0.58) * mm, "end": v(8.72, -0.65) * mm});
            skLineSegment(sketch, "E203", {"start": v(11.5, 7.65) * mm, "end": v(19.4, 19.08) * mm});
            skLineSegment(sketch, "E204.MirrorCS", {"start": v(-10.32, -21.5) * mm, "end": v(-10.73, -21.5) * mm});
            skLineSegment(sketch, "E205.MirrorCS", {"start": v(-29.44, -3.45) * mm, "end": v(-29.4, -3.9) * mm});
            skLineSegment(sketch, "E206.MirrorCS", {"start": v(-3.42, 19.3) * mm, "end": v(-3.9, 19) * mm});
            skLineSegment(sketch, "E207.MirrorCS", {"start": v(-3.97, 15.15) * mm, "end": v(-3.5, 15.16) * mm});
            skLineSegment(sketch, "E208.MirrorCS", {"start": v(-25.69, 34.65) * mm, "end": v(-26.09, 34.38) * mm});
            skLineSegment(sketch, "E209.MirrorCS", {"start": v(-3.9, 19) * mm, "end": v(-3.9, 18.94) * mm});
            skLineSegment(sketch, "E210.MirrorCS", {"start": v(-18.35, 63.84) * mm, "end": v(-18.78, 63.83) * mm});
            skLineSegment(sketch, "E211.MirrorCS", {"start": v(1.64, 6.09) * mm, "end": v(2.05, 4.9) * mm});
            skLineSegment(sketch, "E212.MirrorCS", {"start": v(-20.02, 21.52) * mm, "end": v(-20.65, 21.52) * mm});
            skLineSegment(sketch, "E213.MirrorCS", {"start": v(-11.75, -0.49) * mm, "end": v(-8.25, 4.06) * mm});
            skLineSegment(sketch, "E214.MirrorCS", {"start": v(-9.14, 5.42) * mm, "end": v(-13.23, 0.03) * mm});
            skLineSegment(sketch, "E215.MirrorCS", {"start": v(-18.9, 18.14) * mm, "end": v(-20.02, 21.52) * mm});
            skLineSegment(sketch, "E216.MirrorCS", {"start": v(-16.78, 38.54) * mm, "end": v(-17.65, 39.28) * mm});
            skLineSegment(sketch, "E217.MirrorCS", {"start": v(5.25, 0.63) * mm, "end": v(6.87, -0.63) * mm});
            skLineSegment(sketch, "E218.MirrorCS", {"start": v(-16.4, 33.53) * mm, "end": v(-16.78, 38.54) * mm});
            skLineSegment(sketch, "E219.MirrorCS", {"start": v(0.99, 6.61) * mm, "end": v(1.64, 6.09) * mm});
            skLineSegment(sketch, "E220.MirrorCS", {"start": v(-3.5, 15.16) * mm, "end": v(-2.16, 12.12) * mm});
            skLineSegment(sketch, "E221.MirrorCS", {"start": v(-25.41, 2.28) * mm, "end": v(-25.42, 1.86) * mm});
            skLineSegment(sketch, "E222.MirrorCS", {"start": v(2.05, 4.9) * mm, "end": v(3.59, 1.8) * mm});
            skLineSegment(sketch, "E223.MirrorCS", {"start": v(3.59, 1.8) * mm, "end": v(5.25, 0.63) * mm});
            skLineSegment(sketch, "E224.MirrorCS", {"start": v(-26.72, 40.38) * mm, "end": v(-27.2, 40.37) * mm});
            skLineSegment(sketch, "E225.MirrorCS", {"start": v(-12.54, -6.5) * mm, "end": v(-12.3, -6.65) * mm});
            skLineSegment(sketch, "E226.MirrorCS", {"start": v(-25.42, 1.86) * mm, "end": v(-29.44, -3.45) * mm});
            skLineSegment(sketch, "E227.MirrorCS", {"start": v(-18.83, 55.1) * mm, "end": v(-19.25, 54.75) * mm});
            skLineSegment(sketch, "E228.MirrorCS", {"start": v(-18.78, 63.83) * mm, "end": v(-18.83, 55.1) * mm});
            skLineSegment(sketch, "E229.MirrorCS", {"start": v(-26.09, 34.38) * mm, "end": v(-20.28, 16.81) * mm});
            skLineSegment(sketch, "E230.MirrorCS", {"start": v(-20.28, 16.81) * mm, "end": v(-14.15, 10.64) * mm});
            skLineSegment(sketch, "E231.MirrorCS", {"start": v(-0.64, 8.1) * mm, "end": v(-9.14, 5.42) * mm});
            skLineSegment(sketch, "E232.MirrorCS", {"start": v(-17.65, 39.28) * mm, "end": v(-18.35, 63.84) * mm});
            skLineSegment(sketch, "E233.MirrorCS", {"start": v(4.25, 7.72) * mm, "end": v(-3.42, 19.3) * mm});
            skLineSegment(sketch, "E234.MirrorCS", {"start": v(-12.3, -6.65) * mm, "end": v(-10.73, -21.5) * mm});
            skLineSegment(sketch, "E235.MirrorCS", {"start": v(-10.32, -21.5) * mm, "end": v(-11.75, -0.49) * mm});
            skLineSegment(sketch, "E236.MirrorCS", {"start": v(-0.6, 10.37) * mm, "end": v(-20.72, 7.95) * mm});
            skLineSegment(sketch, "E237.MirrorCS", {"start": v(-27.2, 40.37) * mm, "end": v(-25.69, 34.65) * mm});
            skLineSegment(sketch, "E238.MirrorCS", {"start": v(-20.09, 6.48) * mm, "end": v(-0.64, 8.1) * mm});
            skLineSegment(sketch, "E239.MirrorCS", {"start": v(-14.15, 10.64) * mm, "end": v(-0.6, 10.37) * mm});
            skLineSegment(sketch, "E240.MirrorCS", {"start": v(-13.23, 0.03) * mm, "end": v(-12.54, -6.5) * mm});
            skLineSegment(sketch, "E241.MirrorCS", {"start": v(-10.3, 20.75) * mm, "end": v(-16.4, 33.53) * mm});
            skLineSegment(sketch, "E242.MirrorCS", {"start": v(-3.9, 18.94) * mm, "end": v(-10.3, 20.75) * mm});
            skLineSegment(sketch, "E243.MirrorCS", {"start": v(-20.65, 21.52) * mm, "end": v(-26.72, 40.38) * mm});
            skLineSegment(sketch, "E244.MirrorCS", {"start": v(-2.16, 12.12) * mm, "end": v(-13.27, 13) * mm});
            skLineSegment(sketch, "E245.MirrorCS", {"start": v(-8.25, 4.06) * mm, "end": v(0.99, 6.61) * mm});
            skLineSegment(sketch, "E246.MirrorCS", {"start": v(-29.4, -3.9) * mm, "end": v(-20.09, 6.48) * mm});
            skLineSegment(sketch, "E247.MirrorCS", {"start": v(-19.08, 35.12) * mm, "end": v(-12.37, 19.1) * mm});
            skLineSegment(sketch, "E248.MirrorCS", {"start": v(-13.27, 13) * mm, "end": v(-18.9, 18.14) * mm});
            skLineSegment(sketch, "E249.MirrorCS", {"start": v(-12.37, 19.1) * mm, "end": v(-3.97, 15.15) * mm});
            skLineSegment(sketch, "E250.MirrorCS", {"start": v(-19.25, 54.75) * mm, "end": v(-19.08, 35.12) * mm});
            skLineSegment(sketch, "E251.MirrorCS", {"start": v(-20.72, 7.95) * mm, "end": v(-25.41, 2.28) * mm});
            skLineSegment(sketch, "E252", {"start": v(6.87, -0.63) * mm, "end": v(6.94, 5.86) * mm});
            skLineSegment(sketch, "E253", {"start": v(6.94, 5.86) * mm, "end": v(4.25, 7.72) * mm});
            skLineSegment(sketch, "E254", {"start": v(8.72, -0.65) * mm, "end": v(8.72, 5.83) * mm});
            skLineSegment(sketch, "E255", {"start": v(8.72, 5.83) * mm, "end": v(11.5, 7.65) * mm});
            skSolve(sketch);
        }
        {
            var Q0;
            Q0 = qSketchRegion(id + "F39", true);
            extrude(context, id + "F40", {"entities" : qUnion([Q0]), "operationType" : NewBodyOperationType.REMOVE, "oppositeDirection" : true, "depth" : 25.4 * mm});
        }
    });
